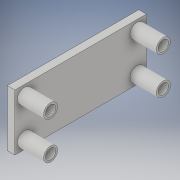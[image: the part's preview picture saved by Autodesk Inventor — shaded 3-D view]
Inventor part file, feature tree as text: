
AUTODESK INVENTOR PART (.ipt)
format: ipt  version: 2019 (Build 230136000, 136)  size: 136,704 bytes
history: native  units: mm
features: extrude x2, sketch x2, other x1
ambient origin geometry x8: Origin, YZ Plane, XZ Plane, XY Plane, X Axis, Y Axis, Z Axis, Center Point
bodies: Body1 (feature_tree)
feature tree (5):
  other  "ソリッド1"
  extrude  "押し出し1"  Depth=60.0mm
  extrude  "押し出し2"  Depth=140.0mm
  sketch  "スケッチ1"
  sketch  "スケッチ2"
